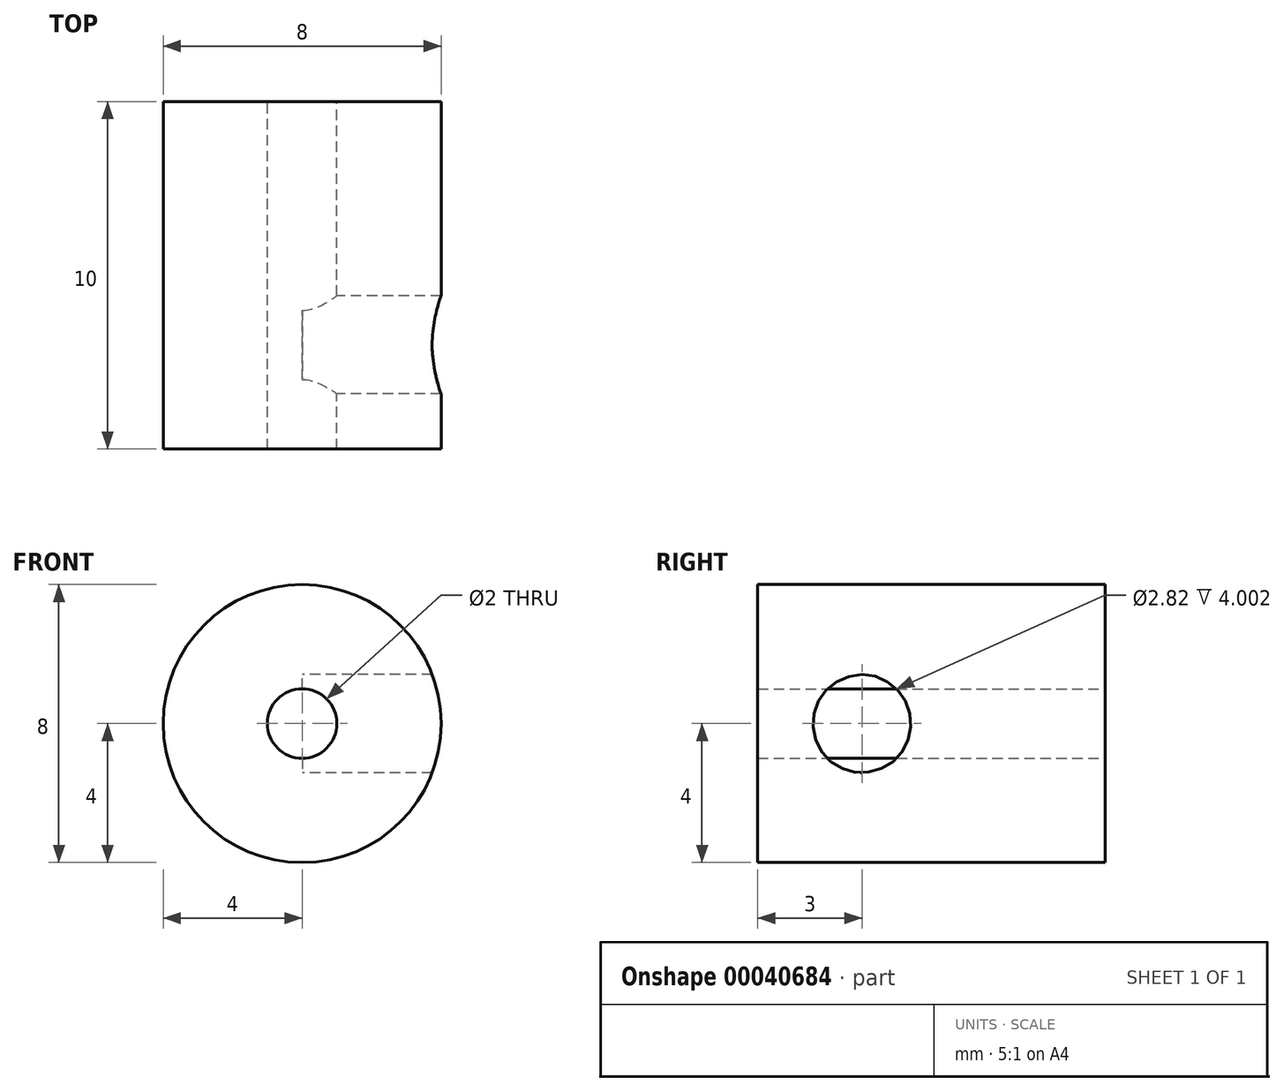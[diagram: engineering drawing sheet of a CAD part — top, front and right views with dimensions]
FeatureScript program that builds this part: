
annotation { "Feature Type Name" : "Feature", "Feature Type Description" : "" }
export const myFeature = defineFeature(function(context is Context, id is Id, definition is map)
    precondition{}
    {
        {
            var Q0;
            Q0=qCreatedBy(makeId("Front.planeOp"),FACE);
            var sketch = newSketch(context, id + "F0", { "sketchPlane" : qUnion([Q0])});
            skCircle(sketch, "E0", {"center": v(0, 0) * mm, "radius": 4 * mm});
            skCircle(sketch, "E1", {"center": v(0, 0) * mm, "radius": 1 * mm});
            skSolve(sketch);
        }
        {
            var Q0;
            Q0=makeQuery(id+"F0.imprint","IMPRINT",FACE,{"disambiguationData":[TD([[makeQuery(id+"F0.imprint","IMPRINT",EDGE,{"derivedFrom":sQuery(id+"F0.wireOp",EDGE,"E0")}),1.0]])]});
            extrude(context, id + "F1", {"entities" : qUnion([Q0]), "depth" : 10 * mm});
        }
        {
            var Q0;
            Q0=qCreatedBy(makeId("Right.planeOp"),FACE);
            var sketch = newSketch(context, id + "F2", { "sketchPlane" : qUnion([Q0])});
            skCircle(sketch, "E2", {"center": v(-7, 0) * mm, "radius": 1.41 * mm});
            skSolve(sketch);
        }
        {
            var Q0;
            Q0 = qSketchRegion(id + "F2", true);
            var Q1;
            Q1=sQuery(id+"F2.wireOp",EDGE,"E2");
            extrude(context, id + "F3", {"entities" : qUnion([Q0]), "operationType" : NewBodyOperationType.REMOVE, "surfaceEntities" : qUnion([Q1]), "depth" : 5 * mm});
        }
    });
